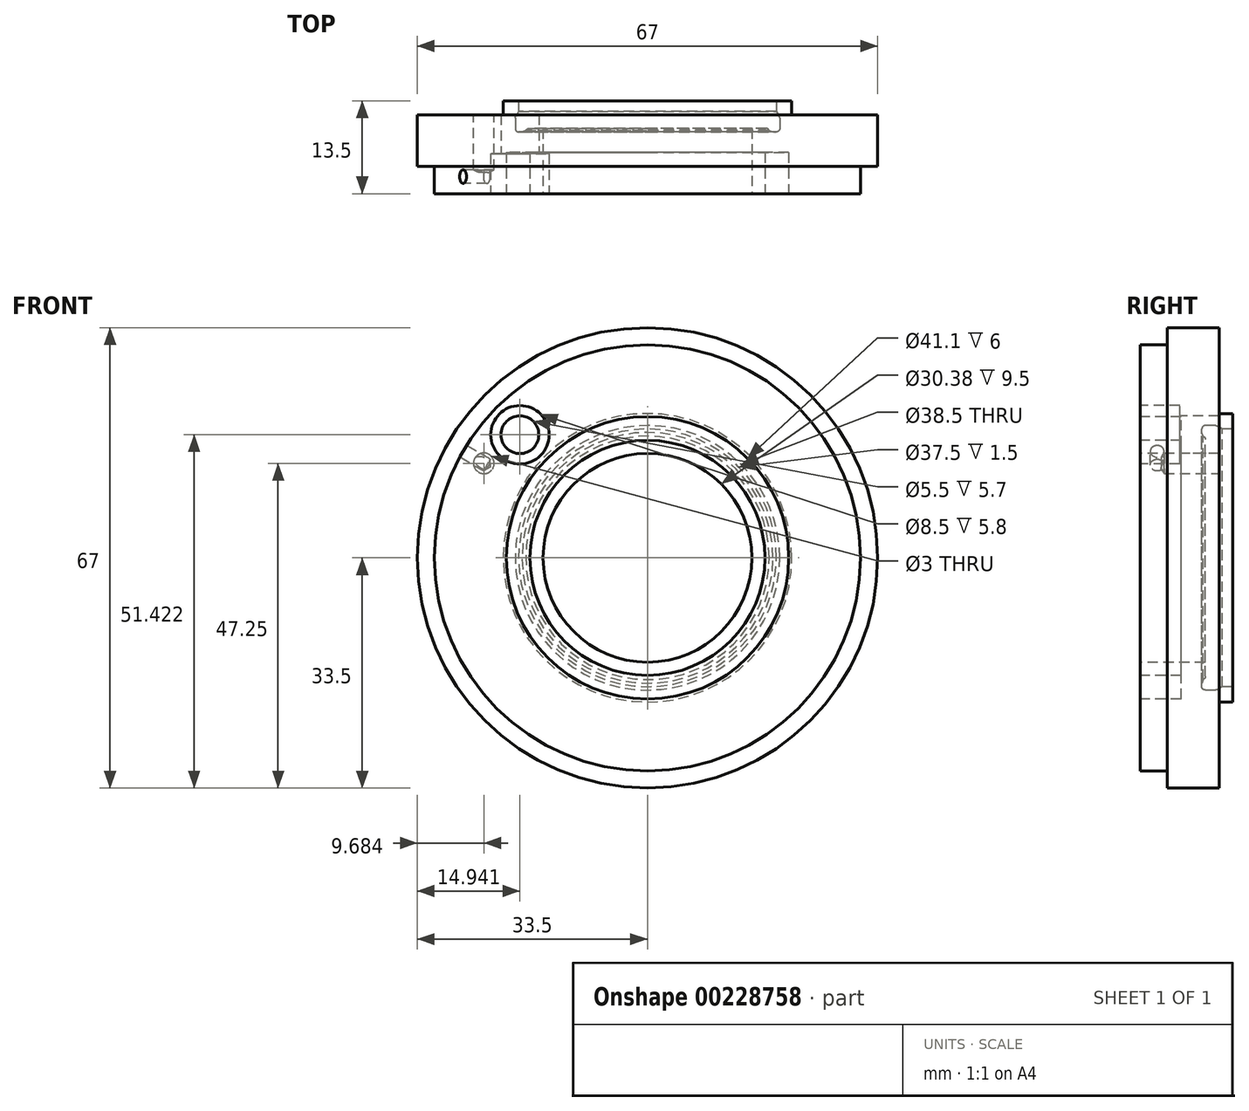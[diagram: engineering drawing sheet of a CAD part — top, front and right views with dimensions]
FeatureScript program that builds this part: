
annotation { "Feature Type Name" : "Feature", "Feature Type Description" : "" }
export const myFeature = defineFeature(function(context is Context, id is Id, definition is map)
    precondition{}
    {
        {
            var Q0;
            Q0=qCreatedBy(makeId("Right.planeOp"),FACE);
            var sketch = newSketch(context, id + "F0", { "sketchPlane" : qUnion([Q0])});
            skLineSegment(sketch, "E0", {"start": v(-7.5, 33.5) * mm, "end": v(0, 33.5) * mm});
            skLineSegment(sketch, "E1", {"start": v(2, 21) * mm, "end": v(2, 18.75) * mm});
            skLineSegment(sketch, "E2", {"start": v(2, 18.75) * mm, "end": v(0.5, 18.75) * mm});
            skLineSegment(sketch, "E3", {"start": v(-2, 17.25) * mm, "end": v(-2, 15.2) * mm});
            skLineSegment(sketch, "E4", {"start": v(-2, 15.2) * mm, "end": v(-11.5, 15.2) * mm});
            skLineSegment(sketch, "E5", {"start": v(-11.5, 15.2) * mm, "end": v(-11.5, 17.1) * mm});
            skLineSegment(sketch, "E6", {"start": v(-11.5, 17.1) * mm, "end": v(-5.5, 17.1) * mm});
            skLineSegment(sketch, "E7", {"start": v(-5.5, 17.1) * mm, "end": v(-5.5, 20.55) * mm});
            skLineSegment(sketch, "E8", {"start": v(-5.5, 20.55) * mm, "end": v(-11.5, 20.55) * mm});
            skLineSegment(sketch, "E9", {"start": v(-11.5, 31) * mm, "end": v(-7.5, 31) * mm});
            skLineSegment(sketch, "E10", {"start": v(-7.5, 31) * mm, "end": v(-7.5, 33.5) * mm});
            skPoint(sketch, "E11.orphan", {"position": v(0, 33.5) * mm});
            skLineSegment(sketch, "E12", {"start": v(-11.5, 31) * mm, "end": v(-11.5, 20.55) * mm});
            skLineSegment(sketch, "E13", {"start": v(0, 33.5) * mm, "end": v(0, 21) * mm});
            skLineSegment(sketch, "E14", {"start": v(0, 21) * mm, "end": v(2, 21) * mm});
            skLineSegment(sketch, "E15", {"start": v(0.5, 18.75) * mm, "end": v(-0.25, 19.18) * mm});
            skLineSegment(sketch, "E16", {"start": v(-0.5, 19.25) * mm, "end": v(-2, 19.25) * mm});
            skLineSegment(sketch, "E17", {"start": v(-2.5, 18.75) * mm, "end": v(-2.5, 18.25) * mm});
            skLineSegment(sketch, "E18", {"start": v(-2.5, 18.25) * mm, "end": v(-2.3, 17.7) * mm});
            skPoint(sketch, "E19.visualSharp", {"position": v(-0.37, 19.25) * mm});
            skArc(sketch, "E19.filletArc", {"start": v(-0.25, 19.18) * mm, "mid": v(-0.37, 19.23) * mm, "end": v(-0.5, 19.25) * mm});
            skPoint(sketch, "E20.visualSharp", {"position": v(-2.5, 19.25) * mm});
            skArc(sketch, "E20.filletArc", {"start": v(-2, 19.25) * mm, "mid": v(-2.35, 19.1) * mm, "end": v(-2.5, 18.75) * mm});
            skArc(sketch, "E21.filletArc", {"start": v(-2, 17.25) * mm, "mid": v(-2.08, 17.53) * mm, "end": v(-2.3, 17.7) * mm});
            skLineSegment(sketch, "E22", {"start": v(-4.24, 0) * mm, "end": v(3.08, 0) * mm});
            skSolve(sketch);
        }
        {
            var Q0;
            Q0=makeQuery(id+"F0.imprint","IMPRINT",FACE,{"disambiguationData":[TD([[makeQuery(id+"F0.imprint","IMPRINT",EDGE,{"derivedFrom":sQuery(id+"F0.wireOp",EDGE,"E0")}),-1.0]])]});
            var Q1;
            Q1=sQuery(id+"F0.wireOp",EDGE,"E22");
            revolve(context, id + "F1", {"entities" : qUnion([Q0]), "axis" : qUnion([Q1]), "revolveType" : RevolveType.FULL});
        }
        {
            var Q0;
            Q0=makeQuery(id+"F1.opRevolve","SWEPT_FACE",FACE,{"disambiguationData":[OSD([sQuery(id+"F0.wireOp",EDGE,"E12")])]});
            var sketch = newSketch(context, id + "F2", { "sketchPlane" : qUnion([Q0])});
            skCircle(sketch, "E23", {"center": v(0, 0) * mm, "radius": 25.8 * mm});
            skLineSegment(sketch, "E24", {"start": v(0, 0) * mm, "end": v(-18.56, 17.92) * mm});
            skPoint(sketch, "E25", {"position": v(-18.56, 17.92) * mm});
            skSolve(sketch);
        }
        {
            var Q0;
            Q0=sQuery(id+"F2.wireOp",VERTEX,"E25");
            var Q1;
            Q1=makeQuery(id+"F1.opRevolve","SWEPT_BODY",BODY,{"disambiguationData":[OSD([sQuery(id+"F0.wireOp",EDGE,"E0"),sQuery(id+"F0.wireOp",EDGE,"E1"),sQuery(id+"F0.wireOp",EDGE,"E2"),sQuery(id+"F0.wireOp",EDGE,"E3"),sQuery(id+"F0.wireOp",EDGE,"E4"),sQuery(id+"F0.wireOp",EDGE,"E5"),sQuery(id+"F0.wireOp",EDGE,"E6"),sQuery(id+"F0.wireOp",EDGE,"E7"),sQuery(id+"F0.wireOp",EDGE,"E8"),sQuery(id+"F0.wireOp",EDGE,"E9"),sQuery(id+"F0.wireOp",EDGE,"E10"),sQuery(id+"F0.wireOp",EDGE,"E12"),sQuery(id+"F0.wireOp",EDGE,"E13"),sQuery(id+"F0.wireOp",EDGE,"E14"),sQuery(id+"F0.wireOp",EDGE,"E15"),sQuery(id+"F0.wireOp",EDGE,"E16"),sQuery(id+"F0.wireOp",EDGE,"E17"),sQuery(id+"F0.wireOp",EDGE,"E19.filletArc"),sQuery(id+"F0.wireOp",EDGE,"E20.filletArc"),sQuery(id+"F0.wireOp",EDGE,"E21.filletArc"),sQuery(id+"F0.wireOp",EDGE,"E18")])]});
            hole(context, id + "F3", {"style" : HoleStyle.C_BORE, "endStyle" : HoleEndStyle.THROUGH, "holeDiameter" : 5.5 * mm, "cBoreDiameter" : 8.5 * mm, "cBoreDepth" : 5.8 * mm, "startFromSketch" : true, "locations" : qUnion([Q0]), "scope" : qUnion([Q1]), "isTappedThrough" : true});
        }
        {
            var Q0;
            Q0=makeQuery(id+"F1.opRevolve","SWEPT_FACE",FACE,{"disambiguationData":[OSD([sQuery(id+"F0.wireOp",EDGE,"E12")])]});
            cPlane(context, id + "F4", {"entities" : qUnion([Q0]), "cplaneType" : CPlaneType.OFFSET, "offset" : 2.5 * mm, "oppositeDirection" : true, "width" : 150 * mm, "height" : 150 * mm});
        }
        {
            var Q0;
            Q0=qCreatedBy(id+"F4.planeOp",FACE);
            var sketch = newSketch(context, id + "F5", { "sketchPlane" : qUnion([Q0])});
            skCircle(sketch, "E26.0", {"center": v(0, 0) * mm, "radius": 31 * mm});
            skLineSegment(sketch, "E27", {"start": v(0, 0) * mm, "end": v(-26.85, 15.5) * mm});
            skPoint(sketch, "E28", {"position": v(-26.85, 15.5) * mm});
            skSolve(sketch);
        }
        {
            var Q0;
            Q0=sQuery(id+"F5.wireOp",EDGE,"E27");
            var Q1;
            Q1=sQuery(id+"F5.wireOp",VERTEX,"E28");
            cPlane(context, id + "F6", {"entities" : qUnion([Q0, Q1]), "cplaneType" : CPlaneType.CURVE_POINT, "offset" : 25 * mm, "width" : 150 * mm, "height" : 150 * mm});
        }
        {
            var Q0;
            Q0=qCreatedBy(id+"F6.planeOp",FACE);
            var sketch = newSketch(context, id + "F7", { "sketchPlane" : qUnion([Q0])});
            skPoint(sketch, "E29.0", {"position": v(9, 0) * mm});
            skSolve(sketch);
        }
        {
            var Q0;
            Q0=sQuery(id+"F7.wireOp",VERTEX,"E29.0");
            var Q1;
            Q1=makeQuery(id+"F1.opRevolve","SWEPT_BODY",BODY,{"disambiguationData":[OSD([sQuery(id+"F0.wireOp",EDGE,"E0"),sQuery(id+"F0.wireOp",EDGE,"E1"),sQuery(id+"F0.wireOp",EDGE,"E2"),sQuery(id+"F0.wireOp",EDGE,"E3"),sQuery(id+"F0.wireOp",EDGE,"E4"),sQuery(id+"F0.wireOp",EDGE,"E5"),sQuery(id+"F0.wireOp",EDGE,"E6"),sQuery(id+"F0.wireOp",EDGE,"E7"),sQuery(id+"F0.wireOp",EDGE,"E8"),sQuery(id+"F0.wireOp",EDGE,"E9"),sQuery(id+"F0.wireOp",EDGE,"E10"),sQuery(id+"F0.wireOp",EDGE,"E12"),sQuery(id+"F0.wireOp",EDGE,"E13"),sQuery(id+"F0.wireOp",EDGE,"E14"),sQuery(id+"F0.wireOp",EDGE,"E15"),sQuery(id+"F0.wireOp",EDGE,"E16"),sQuery(id+"F0.wireOp",EDGE,"E17"),sQuery(id+"F0.wireOp",EDGE,"E19.filletArc"),sQuery(id+"F0.wireOp",EDGE,"E20.filletArc"),sQuery(id+"F0.wireOp",EDGE,"E21.filletArc"),sQuery(id+"F0.wireOp",EDGE,"E18")])]});
            hole(context, id + "F8", {"style" : HoleStyle.SIMPLE, "endStyle" : HoleEndStyle.BLIND, "holeDiameter" : 2 * mm, "holeDepth" : 4 * mm, "startFromSketch" : true, "locations" : qUnion([Q0]), "scope" : qUnion([Q1])});
        }
        {
            var Q0;
            Q0=makeQuery(id+"F1.opRevolve","SWEPT_FACE",FACE,{"disambiguationData":[OSD([sQuery(id+"F0.wireOp",EDGE,"E13")])]});
            var sketch = newSketch(context, id + "F9", { "sketchPlane" : qUnion([Q0])});
            skCircle(sketch, "E30", {"center": v(0, 0) * mm, "radius": 27.5 * mm, "construction": true});
            skLineSegment(sketch, "E31.0", {"start": v(0, 0) * mm, "end": v(26.85, 15.5) * mm, "construction": true});
            skPoint(sketch, "E32", {"position": v(23.82, 13.75) * mm});
            skCircle(sketch, "E33", {"center": v(23.82, 13.75) * mm, "radius": 1.5 * mm});
            skSolve(sketch);
        }
        {
            var Q0;
            Q0=sQuery(id+"F9.wireOp",VERTEX,"E32");
            var Q1;
            Q1=makeQuery(id+"F1.opRevolve","SWEPT_BODY",BODY,{"disambiguationData":[OSD([sQuery(id+"F0.wireOp",EDGE,"E0"),sQuery(id+"F0.wireOp",EDGE,"E1"),sQuery(id+"F0.wireOp",EDGE,"E2"),sQuery(id+"F0.wireOp",EDGE,"E3"),sQuery(id+"F0.wireOp",EDGE,"E4"),sQuery(id+"F0.wireOp",EDGE,"E5"),sQuery(id+"F0.wireOp",EDGE,"E6"),sQuery(id+"F0.wireOp",EDGE,"E7"),sQuery(id+"F0.wireOp",EDGE,"E8"),sQuery(id+"F0.wireOp",EDGE,"E9"),sQuery(id+"F0.wireOp",EDGE,"E10"),sQuery(id+"F0.wireOp",EDGE,"E12"),sQuery(id+"F0.wireOp",EDGE,"E13"),sQuery(id+"F0.wireOp",EDGE,"E14"),sQuery(id+"F0.wireOp",EDGE,"E15"),sQuery(id+"F0.wireOp",EDGE,"E16"),sQuery(id+"F0.wireOp",EDGE,"E17"),sQuery(id+"F0.wireOp",EDGE,"E19.filletArc"),sQuery(id+"F0.wireOp",EDGE,"E20.filletArc"),sQuery(id+"F0.wireOp",EDGE,"E21.filletArc"),sQuery(id+"F0.wireOp",EDGE,"E18")])]});
            hole(context, id + "F10", {"style" : HoleStyle.SIMPLE, "endStyle" : HoleEndStyle.BLIND, "holeDiameter" : 3 * mm, "holeDepth" : 8 * mm, "startFromSketch" : true, "locations" : qUnion([Q0]), "scope" : qUnion([Q1])});
        }
    });
